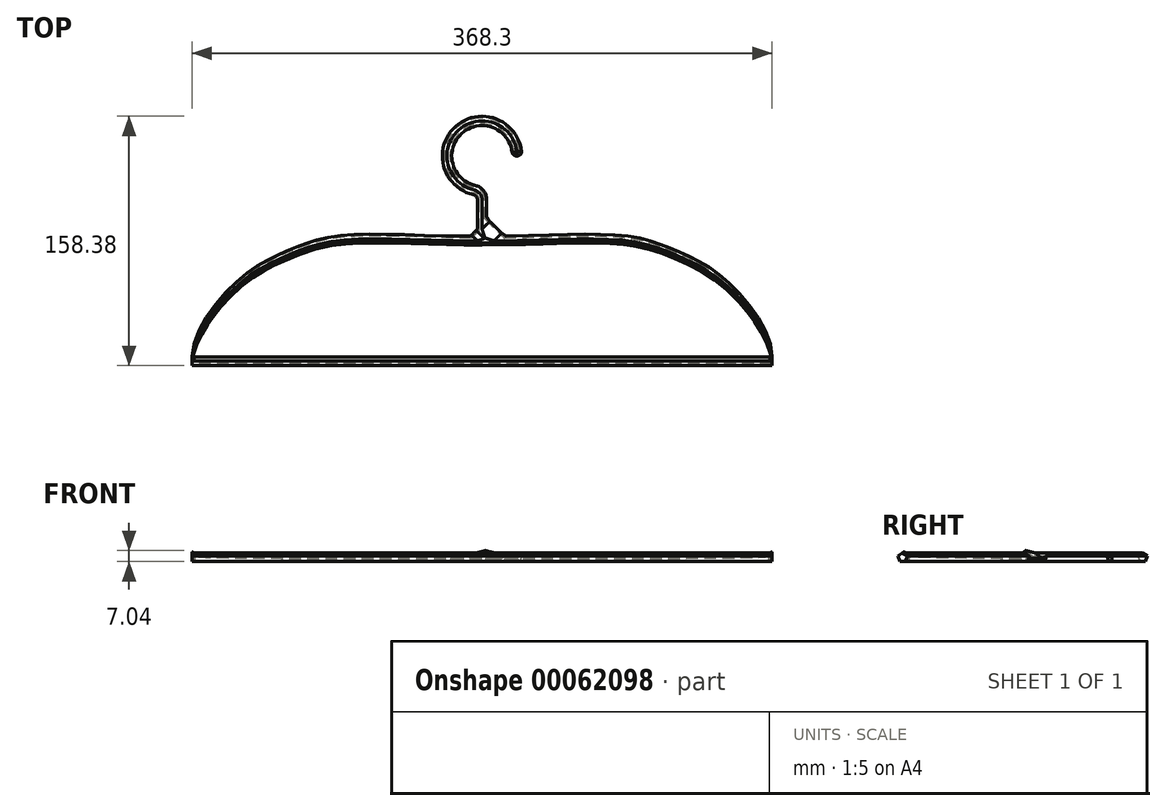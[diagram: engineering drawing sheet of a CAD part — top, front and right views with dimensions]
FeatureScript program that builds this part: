
annotation { "Feature Type Name" : "Feature", "Feature Type Description" : "" }
export const myFeature = defineFeature(function(context is Context, id is Id, definition is map)
    precondition{}
    {
        {
            var Q0;
            Q0=qCreatedBy(makeId("Top.planeOp"),FACE);
            var sketch = newSketch(context, id + "F0", { "sketchPlane" : qUnion([Q0])});
            skLineSegment(sketch, "E0", {"start": v(0, 0) * mm, "end": v(0, 26.11) * mm});
            skArc(sketch, "E1", {"start": v(22.22, 53.98) * mm, "mid": v(-13.86, 71.35) * mm, "end": v(-4.94, 32.3) * mm});
            skLineSegment(sketch, "E2", {"start": v(-184.15, 68.06) * mm, "end": v(-184.15, -76.2) * mm, "construction": true});
            skPoint(sketch, "E3.visualSharp", {"position": v(0, 31.75) * mm});
            skArc(sketch, "E3.filletArc", {"start": v(0, 26.11) * mm, "mid": v(-1.39, 30.07) * mm, "end": v(-4.94, 32.3) * mm});
            skLineSegment(sketch, "E4", {"start": v(-184.15, -76.2) * mm, "end": v(0, -76.2) * mm});
            skFitSpline(sketch, "E5", {"points": [v(-184.15, -76.2) * mm, v(-155.64, -28.65) * mm, v(-124.07, -9.44) * mm, v(-92.74, 0) * mm, v(0, 0) * mm], "startDerivative": vector(1.09, 177.04) * mm, "endDerivative": vector(380.07, 0) * mm});
            skSolve(sketch);
        }
        {
            var Q0;
            Q0=qCreatedBy(makeId("Right.planeOp"),FACE);
            var sketch = newSketch(context, id + "F1", { "sketchPlane" : qUnion([Q0])});
            skCircle(sketch, "E6.cCircle", {"center": v(0, 0) * mm, "radius": 2.54 * mm, "construction": true});
            skLineSegment(sketch, "E6.0", {"start": v(1.85, -2.54) * mm, "end": v(-1.85, -2.54) * mm});
            skLineSegment(sketch, "E6.1", {"start": v(-1.85, -2.54) * mm, "end": v(-2.99, 0.97) * mm});
            skLineSegment(sketch, "E6.2", {"start": v(-2.99, 0.97) * mm, "end": v(0, 3.14) * mm});
            skLineSegment(sketch, "E6.3", {"start": v(0, 3.14) * mm, "end": v(2.99, 0.97) * mm});
            skLineSegment(sketch, "E6.4", {"start": v(2.99, 0.97) * mm, "end": v(1.85, -2.54) * mm});
            skPoint(sketch, "E6.0.midPoint", {"position": v(0, -2.54) * mm});
            skCircle(sketch, "E7.cCircle", {"center": v(-76.2, 0) * mm, "radius": 2.54 * mm, "construction": true});
            skLineSegment(sketch, "E7.0", {"start": v(-74.35, -2.54) * mm, "end": v(-78.05, -2.54) * mm});
            skLineSegment(sketch, "E7.1", {"start": v(-78.05, -2.54) * mm, "end": v(-79.19, 0.97) * mm});
            skLineSegment(sketch, "E7.2", {"start": v(-79.19, 0.97) * mm, "end": v(-76.2, 3.14) * mm});
            skLineSegment(sketch, "E7.3", {"start": v(-76.2, 3.14) * mm, "end": v(-73.21, 0.97) * mm});
            skLineSegment(sketch, "E7.4", {"start": v(-73.21, 0.97) * mm, "end": v(-74.35, -2.54) * mm});
            skPoint(sketch, "E7.0.midPoint", {"position": v(-76.2, -2.54) * mm});
            skSolve(sketch);
        }
        {
            var Q0;
            Q0=makeQuery(id+"F1.imprint","IMPRINT",FACE,{"disambiguationData":[TD([[makeQuery(id+"F1.imprint","IMPRINT",EDGE,{"derivedFrom":sQuery(id+"F1.wireOp",EDGE,"E6.0")}),-1.0]])]});
            var Q1;
            Q1=sQuery(id+"F0.wireOp",EDGE,"Gh1WaK53-GoLn-ul4y-smVX-wlRbIqy4xVIt");
            var Q2;
            Q2=sQuery(id+"F0.wireOp",EDGE,"E5");
            sweep(context, id + "F2", {"profiles" : qUnion([Q0]), "path" : qUnion([Q1, Q2]), "keepProfileOrientation" : true});
        }
        {
            var Q0;
            Q0=qCreatedBy(makeId("Front.planeOp"),FACE);
            var sketch = newSketch(context, id + "F3", { "sketchPlane" : qUnion([Q0])});
            skCircle(sketch, "E8.cCircle", {"center": v(0, 0) * mm, "radius": 2.54 * mm, "construction": true});
            skLineSegment(sketch, "E8.0", {"start": v(1.85, -2.54) * mm, "end": v(-1.85, -2.54) * mm});
            skLineSegment(sketch, "E8.1", {"start": v(-1.85, -2.54) * mm, "end": v(-2.99, 0.97) * mm});
            skLineSegment(sketch, "E8.2", {"start": v(-2.99, 0.97) * mm, "end": v(0, 3.14) * mm});
            skLineSegment(sketch, "E8.3", {"start": v(0, 3.14) * mm, "end": v(2.99, 0.97) * mm});
            skLineSegment(sketch, "E8.4", {"start": v(2.99, 0.97) * mm, "end": v(1.85, -2.54) * mm});
            skPoint(sketch, "E8.0.midPoint", {"position": v(0, -2.54) * mm});
            skSolve(sketch);
        }
        {
            var Q0;
            Q0=makeQuery(id+"F3.imprint","IMPRINT",FACE,{"disambiguationData":[TD([[makeQuery(id+"F3.imprint","IMPRINT",EDGE,{"derivedFrom":sQuery(id+"F3.wireOp",EDGE,"E8.0")}),-1.0]])]});
            var Q1;
            Q1=sQuery(id+"F0.wireOp",EDGE,"E3.filletArc");
            var Q2;
            Q2=sQuery(id+"F0.wireOp",EDGE,"E1");
            var Q3;
            Q3=sQuery(id+"F0.wireOp",EDGE,"E0");
            sweep(context, id + "F4", {"profiles" : qUnion([Q0]), "path" : qUnion([Q1, Q2, Q3])});
        }
        {
            var Q0;
            Q0=makeQuery(id+"F1.imprint","IMPRINT",FACE,{"disambiguationData":[TD([[makeQuery(id+"F1.imprint","IMPRINT",EDGE,{"derivedFrom":sQuery(id+"F1.wireOp",EDGE,"E7.0")}),-1.0]])]});
            var Q1;
            Q1=sQuery(id+"F0.wireOp",EDGE,"E4");
            sweep(context, id + "F5", {"operationType" : NewBodyOperationType.ADD, "profiles" : qUnion([Q0]), "path" : qUnion([Q1])});
        }
        {
            var Q0;
            Q0=makeQuery(id+"F5.boolean.opBoolean","INTERSECT",EDGE,{"derivedFrom":[makeQuery(id+"F2.opSweep","SWEPT_FACE",FACE,{"disambiguationData":[OSD([sQuery(id+"F0.wireOp",EDGE,"E5"),sQuery(id+"F1.wireOp",EDGE,"E6.2")])]}),makeQuery(id+"F5.opSweep","SWEPT_FACE",FACE,{"disambiguationData":[OSD([sQuery(id+"F0.wireOp",EDGE,"E4"),sQuery(id+"F1.wireOp",EDGE,"E7.3")])]})]});
            var Q1;
            Q1=makeQuery(id+"F5.boolean.opBoolean","INTERSECT",EDGE,{"derivedFrom":[makeQuery(id+"F2.opSweep","SWEPT_FACE",FACE,{"disambiguationData":[OSD([sQuery(id+"F0.wireOp",EDGE,"E5"),sQuery(id+"F1.wireOp",EDGE,"E6.1")])]}),makeQuery(id+"F5.opSweep","SWEPT_FACE",FACE,{"disambiguationData":[OSD([sQuery(id+"F0.wireOp",EDGE,"E4"),sQuery(id+"F1.wireOp",EDGE,"E7.4")])]})]});
            fillet(context, id + "F6", {"entities" : qUnion([Q0, Q1]), "radius" : 1.27 * mm, "tangentPropagation" : true, "allowEdgeOverflow" : false});
        }
        {
            var Q0;
            Q0=makeQuery(id+"F2.opSweep","SWEPT_BODY",BODY,{"disambiguationData":[OSD([sQuery(id+"F0.wireOp",EDGE,"Gh1WaK53-GoLn-ul4y-smVX-wlRbIqy4xVIt"),sQuery(id+"F1.wireOp",EDGE,"E6.0"),sQuery(id+"F1.wireOp",EDGE,"E6.1"),sQuery(id+"F1.wireOp",EDGE,"E6.2"),sQuery(id+"F1.wireOp",EDGE,"E6.3"),sQuery(id+"F1.wireOp",EDGE,"E6.4")])]});
            var Q1;
            Q1=qCreatedBy(makeId("Right.planeOp"),FACE);
            mirror(context, id + "F7", {"entities" : qUnion([Q0]), "mirrorPlane" : qUnion([Q1])});
        }
        {
            var Q0;
            Q0=makeQuery(id+"F4.opSweep","SWEPT_BODY",BODY,{"disambiguationData":[OSD([sQuery(id+"F0.wireOp",EDGE,"E0"),sQuery(id+"F3.wireOp",EDGE,"E8.0"),sQuery(id+"F3.wireOp",EDGE,"E8.1"),sQuery(id+"F3.wireOp",EDGE,"E8.2"),sQuery(id+"F3.wireOp",EDGE,"E8.3"),sQuery(id+"F3.wireOp",EDGE,"E8.4")])]});
            var Q1;
            Q1=makeQuery(id+"F2.opSweep","SWEPT_BODY",BODY,{"disambiguationData":[OSD([sQuery(id+"F0.wireOp",EDGE,"Gh1WaK53-GoLn-ul4y-smVX-wlRbIqy4xVIt"),sQuery(id+"F1.wireOp",EDGE,"E6.0"),sQuery(id+"F1.wireOp",EDGE,"E6.1"),sQuery(id+"F1.wireOp",EDGE,"E6.2"),sQuery(id+"F1.wireOp",EDGE,"E6.3"),sQuery(id+"F1.wireOp",EDGE,"E6.4")])]});
            var Q2;
            Q2=makeQuery(id+"F7.opPattern","COPY",BODY,{"derivedFrom":makeQuery(id+"F2.opSweep","SWEPT_BODY",BODY,{"disambiguationData":[OSD([sQuery(id+"F0.wireOp",EDGE,"Gh1WaK53-GoLn-ul4y-smVX-wlRbIqy4xVIt"),sQuery(id+"F1.wireOp",EDGE,"E6.0"),sQuery(id+"F1.wireOp",EDGE,"E6.1"),sQuery(id+"F1.wireOp",EDGE,"E6.2"),sQuery(id+"F1.wireOp",EDGE,"E6.3"),sQuery(id+"F1.wireOp",EDGE,"E6.4")])]}),"instanceName":"1"});
            booleanBodies(context, id + "F8", {"operationType" : BooleanOperationType.UNION, "tools" : qUnion([Q0, Q1, Q2]), "keepTools" : true});
        }
        {
            var Q0;
            Q0=makeQuery(id+"F4.opSweep","CAP_EDGE",EDGE,{"disambiguationData":[OSD([sQuery(id+"F0.wireOp",VERTEX,"E1.start"),sQuery(id+"F3.wireOp",EDGE,"079b0d4f-e7cb-407d-a380-d36e278eac54")])],"isStart":false});
            fillet(context, id + "F9", {"entities" : qUnion([Q0]), "radius" : 2.54 * mm, "tangentPropagation" : true, "allowEdgeOverflow" : false});
        }
        {
            var Q0;
            Q0=makeQuery(id+"F8.opBoolean","INTERSECT",EDGE,{"derivedFrom":[makeQuery(id+"F2.opSweep","SWEPT_FACE",FACE,{"disambiguationData":[OSD([sQuery(id+"F0.wireOp",EDGE,"Gh1WaK53-GoLn-ul4y-smVX-wlRbIqy4xVIt"),sQuery(id+"F1.wireOp",EDGE,"E6.3")])]}),makeQuery(id+"F4.opSweep","SWEPT_FACE",FACE,{"disambiguationData":[OSD([sQuery(id+"F0.wireOp",EDGE,"E0"),sQuery(id+"F3.wireOp",EDGE,"E8.2")])]})]});
            var Q1;
            Q1=makeQuery(id+"F8.opBoolean","INTERSECT",EDGE,{"derivedFrom":[makeQuery(id+"F2.opSweep","SWEPT_FACE",FACE,{"disambiguationData":[OSD([sQuery(id+"F0.wireOp",EDGE,"Gh1WaK53-GoLn-ul4y-smVX-wlRbIqy4xVIt"),sQuery(id+"F1.wireOp",EDGE,"E6.4")])]}),makeQuery(id+"F4.opSweep","SWEPT_FACE",FACE,{"disambiguationData":[OSD([sQuery(id+"F0.wireOp",EDGE,"E0"),sQuery(id+"F3.wireOp",EDGE,"E8.1")])]})]});
            chamfer(context, id + "F10", {"entities" : qUnion([Q0, Q1]), "width" : 5.08 * mm, "tangentPropagation" : true});
        }
        {
            var Q0;
            Q0=makeQuery(id+"F8.opBoolean","INTERSECT",EDGE,{"derivedFrom":[makeQuery(id+"F4.opSweep","SWEPT_FACE",FACE,{"disambiguationData":[OSD([sQuery(id+"F0.wireOp",EDGE,"E0"),sQuery(id+"F3.wireOp",EDGE,"E8.3")])]}),makeQuery(id+"F7.opPattern","COPY",FACE,{"derivedFrom":makeQuery(id+"F2.opSweep","SWEPT_FACE",FACE,{"disambiguationData":[OSD([sQuery(id+"F0.wireOp",EDGE,"Gh1WaK53-GoLn-ul4y-smVX-wlRbIqy4xVIt"),sQuery(id+"F1.wireOp",EDGE,"E6.3")])]}),"instanceName":"1"})]});
            var Q1;
            Q1=makeQuery(id+"F8.opBoolean","INTERSECT",EDGE,{"derivedFrom":[makeQuery(id+"F4.opSweep","SWEPT_FACE",FACE,{"disambiguationData":[OSD([sQuery(id+"F0.wireOp",EDGE,"E0"),sQuery(id+"F3.wireOp",EDGE,"E8.4")])]}),makeQuery(id+"F7.opPattern","COPY",FACE,{"derivedFrom":makeQuery(id+"F2.opSweep","SWEPT_FACE",FACE,{"disambiguationData":[OSD([sQuery(id+"F0.wireOp",EDGE,"Gh1WaK53-GoLn-ul4y-smVX-wlRbIqy4xVIt"),sQuery(id+"F1.wireOp",EDGE,"E6.4")])]}),"instanceName":"1"})]});
            chamfer(context, id + "F11", {"entities" : qUnion([Q0, Q1]), "width" : 12.7 * mm, "tangentPropagation" : true});
        }
        {
            var Q0;
            {var subQ0=makeQuery(id+"F5.opSweep","SWEPT_EDGE",EDGE,{"disambiguationData":[OSD([sQuery(id+"F0.wireOp",EDGE,"E4"),sQuery(id+"F1.wireOp",EDGE,"E7.3"),sQuery(id+"F1.wireOp",EDGE,"E7.4")])]});Q0=makeQuery(id+"F8.opBoolean","MERGE",EDGE,{"derivedFrom":[subQ0,makeQuery(id+"F7.opPattern","COPY",EDGE,{"derivedFrom":subQ0,"instanceName":"1"})]});}
            fillet(context, id + "F12", {"entities" : qUnion([Q0]), "radius" : 2.54 * mm, "tangentPropagation" : true, "allowEdgeOverflow" : false});
        }
    });
